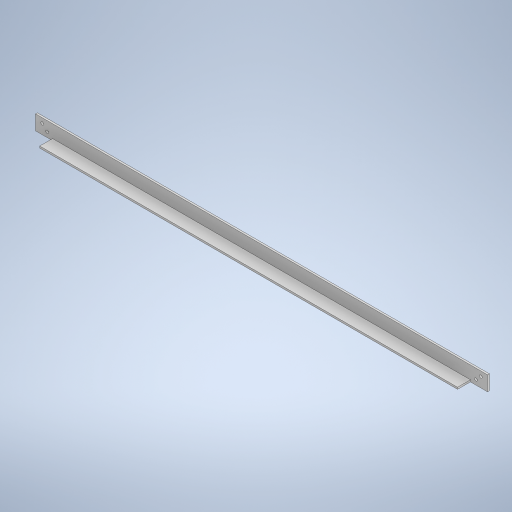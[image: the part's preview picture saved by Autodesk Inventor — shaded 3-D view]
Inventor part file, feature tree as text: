
AUTODESK INVENTOR PART (.ipt)
format: ipt  version: 2023 (Build 270158000, 158)  size: 285,696 bytes
history: native  units: in
note: dims shown in document units (in); Inventor stores cm internally (conversion verified against a paired STEP export)
features: extrude x3, sketch x3, mirror x1
ambient origin geometry x8: Origin, YZ Plane, XZ Plane, XY Plane, X Axis, Y Axis, Z Axis, Center Point
bodies: Solid1 (feature_tree)
feature tree (7):
  extrude  "Extrusion1"  Depth=0.125in
  extrude  "Extrusion2"  TaperAngle=0.0deg  [1 undecoded]
  sketch  "Sketch3"  dims[d5=1.1644in d6=0.125in d7=0.0in d14=0.125in d15=1.0in d16=0.3333in d17=0.191in d18=0.125in d19=0.0in]
  extrude  "Extrusion4"  Depth=0.125in
  mirror  "Mirror2"
  sketch  "Sketch1"  dims[d1=1.0in d2=0.125in]
  sketch  "Sketch2"  dims[d3=30.7539in d4=0.0in]
note: 1 required parameter value undecoded (feature->parameter linkage not recoverable at this tier; creation-order binding heuristic only, values carry confidence <= 0.55)
